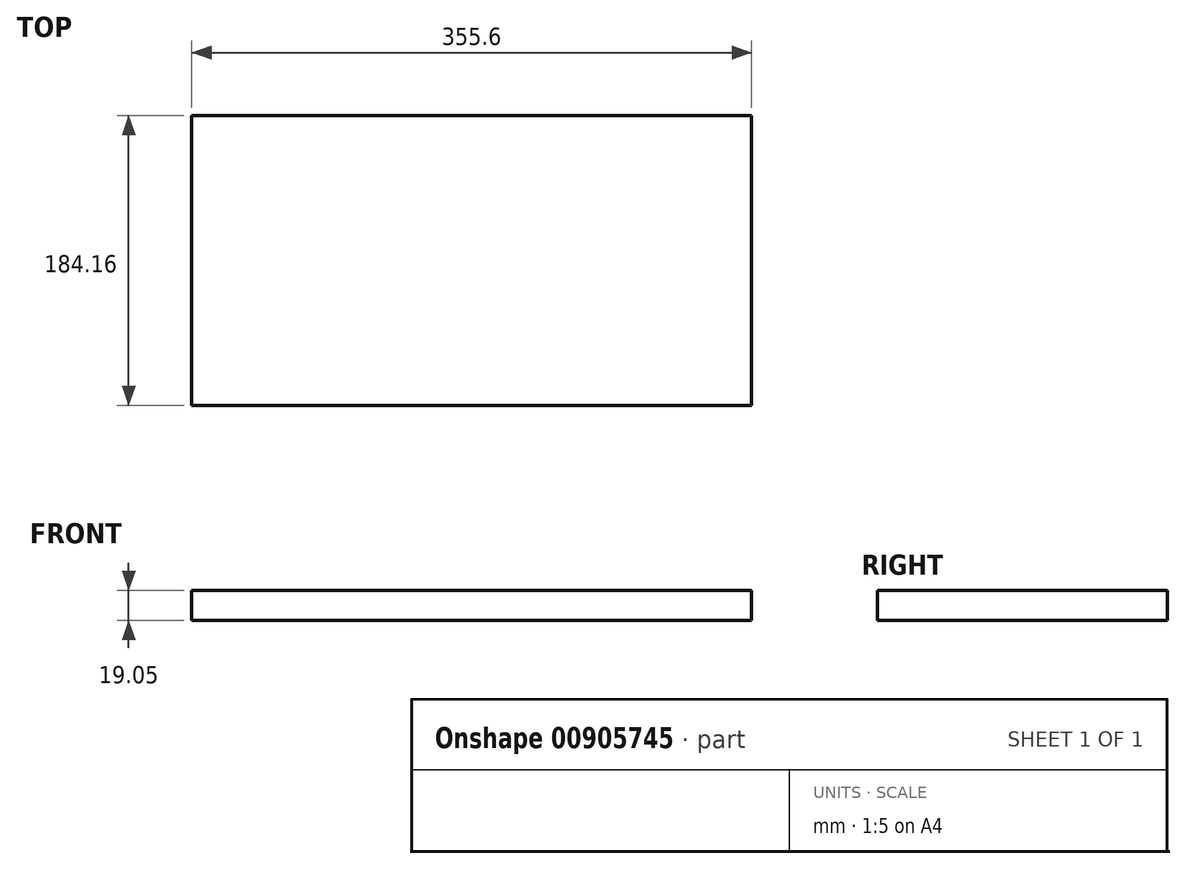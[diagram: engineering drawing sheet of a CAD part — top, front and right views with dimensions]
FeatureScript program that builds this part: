
annotation { "Feature Type Name" : "Feature", "Feature Type Description" : "" }
export const myFeature = defineFeature(function(context is Context, id is Id, definition is map)
    precondition{}
    {
        {
            var Q0;
            Q0=qCreatedBy(makeId("Top.planeOp"),FACE);
            var sketch = newSketch(context, id + "F0", { "sketchPlane" : qUnion([Q0])});
            skLineSegment(sketch, "E0.bottom", {"start": v(177.8, 92.08) * mm, "end": v(-177.8, 92.08) * mm});
            skLineSegment(sketch, "E0.top", {"start": v(177.8, -92.08) * mm, "end": v(-177.8, -92.08) * mm});
            skLineSegment(sketch, "E0.left", {"start": v(177.8, 92.08) * mm, "end": v(177.8, -92.08) * mm});
            skLineSegment(sketch, "E0.right", {"start": v(-177.8, 92.08) * mm, "end": v(-177.8, -92.08) * mm});
            skPoint(sketch, "E0.middle", {"position": v(0, 0) * mm});
            skSolve(sketch);
        }
        {
            var Q0;
            Q0 = qSketchRegion(id + "F0", true);
            extrude(context, id + "F1", {"entities" : qUnion([Q0]), "depth" : 19.05 * mm, "offsetDistance" : 25.4 * mm});
        }
    });
